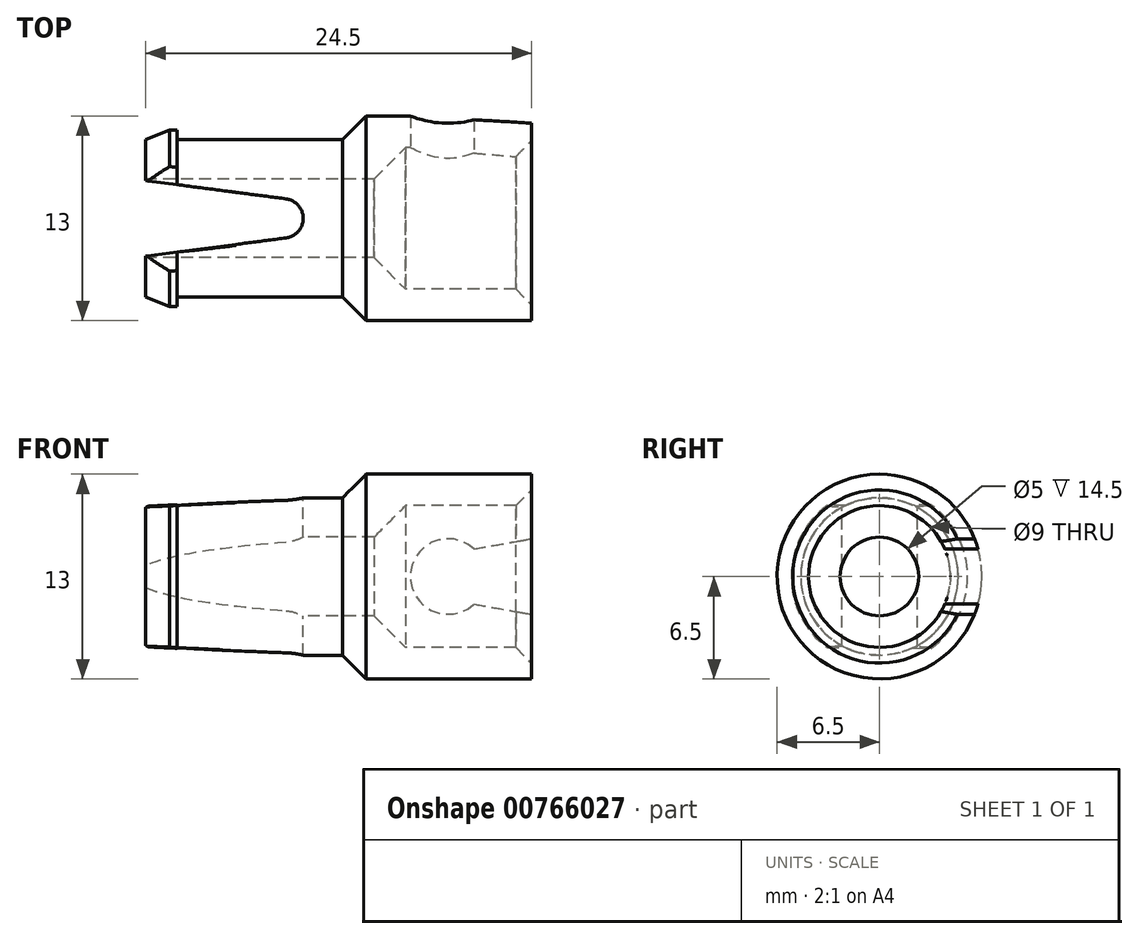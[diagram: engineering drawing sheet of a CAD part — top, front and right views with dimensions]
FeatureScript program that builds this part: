
annotation { "Feature Type Name" : "Feature", "Feature Type Description" : "" }
export const myFeature = defineFeature(function(context is Context, id is Id, definition is map)
    precondition{}
    {
        {
            var Q0;
            Q0=qCreatedBy(makeId("Front.planeOp"),FACE);
            var sketch = newSketch(context, id + "F0", { "sketchPlane" : qUnion([Q0])});
            skLineSegment(sketch, "E0", {"start": v(-22.5, 5) * mm, "end": v(-12, 5) * mm});
            skLineSegment(sketch, "E1", {"start": v(-12, 5) * mm, "end": v(-10.5, 6.5) * mm});
            skLineSegment(sketch, "E2", {"start": v(-10.5, 6.5) * mm, "end": v(0, 6.5) * mm});
            skLineSegment(sketch, "E3", {"start": v(0, 6.5) * mm, "end": v(0, 5.5) * mm});
            skLineSegment(sketch, "E4", {"start": v(0, 5.5) * mm, "end": v(-1, 4.5) * mm});
            skLineSegment(sketch, "E5", {"start": v(-1, 4.5) * mm, "end": v(-8, 4.5) * mm});
            skLineSegment(sketch, "E6", {"start": v(-8, 4.5) * mm, "end": v(-10, 2.5) * mm});
            skLineSegment(sketch, "E7", {"start": v(-10, 2.5) * mm, "end": v(-24.5, 2.5) * mm});
            skLineSegment(sketch, "E8", {"start": v(-22.73, 0) * mm, "end": v(22.26, 0) * mm, "construction": true});
            skLineSegment(sketch, "E9", {"start": v(-22.5, 5) * mm, "end": v(-22.5, 5.6) * mm});
            skLineSegment(sketch, "E10", {"start": v(-22.5, 5.6) * mm, "end": v(-23, 5.6) * mm});
            skLineSegment(sketch, "E11", {"start": v(-23, 5.6) * mm, "end": v(-24.5, 5) * mm});
            skLineSegment(sketch, "E12", {"start": v(-24.5, 5) * mm, "end": v(-24.5, 2.5) * mm});
            skSolve(sketch);
        }
        {
            var Q0;
            Q0=makeQuery(id+"F0.imprint","IMPRINT",FACE,{"disambiguationData":[TD([[makeQuery(id+"F0.imprint","IMPRINT",EDGE,{"derivedFrom":sQuery(id+"F0.wireOp",EDGE,"E0")}),-1.0]])]});
            var Q1;
            Q1=sQuery(id+"F0.wireOp",EDGE,"E8");
            revolve(context, id + "F1", {"surfaceOperationType" : NewSurfaceOperationType.NEW, "entities" : qUnion([Q0]), "axis" : qUnion([Q1]), "revolveType" : RevolveType.FULL});
        }
        {
            var Q0;
            Q0=qCreatedBy(makeId("Front.planeOp"),FACE);
            var sketch = newSketch(context, id + "F2", { "sketchPlane" : qUnion([Q0])});
            skLineSegment(sketch, "E13.0", {"start": v(-12, -5) * mm, "end": v(-12, 5) * mm, "construction": true});
            skLineSegment(sketch, "E14", {"start": v(-10.5, 6.5) * mm, "end": v(0, 6.5) * mm, "construction": true});
            skLineSegment(sketch, "E15", {"start": v(0, -6.5) * mm, "end": v(-10.5, -6.5) * mm, "construction": true});
            skArc(sketch, "E16", {"start": v(-3.66, 1.75) * mm, "mid": v(-7.7, 0) * mm, "end": v(-3.66, -1.75) * mm});
            skPoint(sketch, "E17", {"position": v(-12, 0) * mm});
            skLineSegment(sketch, "E18", {"start": v(-3.66, 1.75) * mm, "end": v(0, 2.4) * mm});
            skLineSegment(sketch, "E19", {"start": v(-3.66, -1.75) * mm, "end": v(0, -2.4) * mm});
            skLineSegment(sketch, "E20", {"start": v(0, 2.4) * mm, "end": v(0, -2.4) * mm});
            skPoint(sketch, "E21", {"position": v(0, 0) * mm});
            skSolve(sketch);
        }
        {
            var Q0;
            Q0 = qSketchRegion(id + "F2", true);
            extrude(context, id + "F3", {"entities" : qUnion([Q0]), "operationType" : NewBodyOperationType.REMOVE, "endBound" : BoundingType.THROUGH_ALL, "oppositeDirection" : true, "depth" : 25 * mm, "offsetDistance" : 25 * mm});
        }
        {
            var Q0;
            Q0=qCreatedBy(makeId("Top.planeOp"),FACE);
            var sketch = newSketch(context, id + "F4", { "sketchPlane" : qUnion([Q0])});
            skLineSegment(sketch, "E22.0", {"start": v(-24.5, -5) * mm, "end": v(-24.5, 5) * mm, "construction": true});
            skLineSegment(sketch, "E23", {"start": v(-24.5, 2.4) * mm, "end": v(-24.5, -2.4) * mm});
            skPoint(sketch, "E24", {"position": v(-24.5, 0) * mm});
            skArc(sketch, "E25", {"start": v(-15.59, -1.24) * mm, "mid": v(-14.5, 0) * mm, "end": v(-15.59, 1.24) * mm});
            skLineSegment(sketch, "E26", {"start": v(-24.5, 2.4) * mm, "end": v(-15.59, 1.24) * mm});
            skLineSegment(sketch, "E27", {"start": v(-24.5, -2.4) * mm, "end": v(-15.59, -1.24) * mm});
            skSolve(sketch);
        }
        {
            var Q0;
            Q0=makeQuery(id+"F4.imprint","IMPRINT",FACE,{"disambiguationData":[TD([[makeQuery(id+"F4.imprint","IMPRINT",EDGE,{"derivedFrom":sQuery(id+"F4.wireOp",EDGE,"E23")}),1.0]])]});
            extrude(context, id + "F5", {"entities" : qUnion([Q0]), "operationType" : NewBodyOperationType.REMOVE, "endBound" : BoundingType.SYMMETRIC, "oppositeDirection" : true, "depth" : 100 * mm, "offsetDistance" : 25 * mm});
        }
        {
            var Q0;
            Q0=makeQuery(id+"F5.boolean.opBoolean","INTERSECT",EDGE,{"disambiguationData":[OD(0.0)],"derivedFrom":[makeQuery(id+"F1.opRevolve","SWEPT_FACE",FACE,{"disambiguationData":[OSD([sQuery(id+"F0.wireOp",EDGE,"E0")])]}),makeQuery(id+"F5.opExtrude","SWEPT_FACE",FACE,{"disambiguationData":[OSD([sQuery(id+"F4.wireOp",EDGE,"E26")])]})]});
            cPoint(context, id + "F6", {"entities" : qUnion([Q0]), "parameter" : 0.5});
        }
        {
            var Q0;
            Q0=makeQuery(id+"F5.boolean.opBoolean","INTERSECT",VERTEX,{"disambiguationData":[OD(0.0)],"derivedFrom":[makeQuery(id+"F1.opRevolve","SWEPT_FACE",FACE,{"disambiguationData":[OSD([sQuery(id+"F0.wireOp",EDGE,"E0")])]}),makeQuery(id+"F1.opRevolve","SWEPT_FACE",FACE,{"disambiguationData":[OSD([sQuery(id+"F0.wireOp",EDGE,"E9")])]}),makeQuery(id+"F5.opExtrude","SWEPT_FACE",FACE,{"disambiguationData":[OSD([sQuery(id+"F4.wireOp",EDGE,"E27")])]})]});
            var Q1;
            Q1 = qCreatedBy(id + "F6" ,VERTEX);
            var Q2;
            Q2=makeQuery(id+"F5.boolean.opBoolean","INTERSECT",VERTEX,{"disambiguationData":[OD(0.0)],"derivedFrom":[makeQuery(id+"F1.opRevolve","SWEPT_FACE",FACE,{"disambiguationData":[OSD([sQuery(id+"F0.wireOp",EDGE,"E0")])]}),makeQuery(id+"F5.opExtrude","SWEPT_FACE",FACE,{"disambiguationData":[OSD([sQuery(id+"F4.wireOp",EDGE,"E25")])]}),makeQuery(id+"F5.opExtrude","SWEPT_FACE",FACE,{"disambiguationData":[OSD([sQuery(id+"F4.wireOp",EDGE,"E27")])]})]});
            cPlane(context, id + "F7", {"entities" : qUnion([Q0, Q1, Q2]), "cplaneType" : CPlaneType.THREE_POINT, "offset" : 25 * mm, "width" : 150 * mm, "height" : 150 * mm});
        }
        {
            var Q0;
            Q0=qCreatedBy(id+"F7.planeOp",FACE);
            var sketch = newSketch(context, id + "F8", { "sketchPlane" : qUnion([Q0])});
            skLineSegment(sketch, "E28.bottom", {"start": v(-19.4, -3.89) * mm, "end": v(-28.8, -3.89) * mm});
            skLineSegment(sketch, "E28.top", {"start": v(-19.4, 5.94) * mm, "end": v(-28.8, 5.94) * mm});
            skLineSegment(sketch, "E28.left", {"start": v(-19.4, -3.89) * mm, "end": v(-19.4, 5.94) * mm});
            skLineSegment(sketch, "E28.right", {"start": v(-28.8, -3.89) * mm, "end": v(-28.8, 5.94) * mm});
            skSolve(sketch);
        }
        {
            var Q0;
            Q0=makeQuery(id+"F8.imprint","IMPRINT",FACE,{"disambiguationData":[TD([[makeQuery(id+"F8.imprint","IMPRINT",EDGE,{"derivedFrom":sQuery(id+"F8.wireOp",EDGE,"E28.bottom")}),-1.0]])]});
            extrude(context, id + "F9", {"entities" : qUnion([Q0]), "operationType" : NewBodyOperationType.REMOVE, "oppositeDirection" : true, "depth" : 25 * mm, "offsetDistance" : 25 * mm});
        }
        {
            var Q0;
            Q0=makeQuery(id+"F5.boolean.opBoolean","INTERSECT",EDGE,{"disambiguationData":[OD(1.0)],"derivedFrom":[makeQuery(id+"F1.opRevolve","SWEPT_FACE",FACE,{"disambiguationData":[OSD([sQuery(id+"F0.wireOp",EDGE,"E0")])]}),makeQuery(id+"F5.opExtrude","SWEPT_FACE",FACE,{"disambiguationData":[OSD([sQuery(id+"F4.wireOp",EDGE,"E26")])]})]});
            cPoint(context, id + "F10", {"entities" : qUnion([Q0]), "parameter" : 0.5});
        }
        {
            var Q0;
            Q0=makeQuery(id+"F5.boolean.opBoolean","INTERSECT",VERTEX,{"disambiguationData":[OD(1.0)],"derivedFrom":[makeQuery(id+"F1.opRevolve","SWEPT_FACE",FACE,{"disambiguationData":[OSD([sQuery(id+"F0.wireOp",EDGE,"E0")])]}),makeQuery(id+"F1.opRevolve","SWEPT_FACE",FACE,{"disambiguationData":[OSD([sQuery(id+"F0.wireOp",EDGE,"E9")])]}),makeQuery(id+"F5.opExtrude","SWEPT_FACE",FACE,{"disambiguationData":[OSD([sQuery(id+"F4.wireOp",EDGE,"E27")])]})]});
            var Q1;
            Q1=makeQuery(id+"F5.boolean.opBoolean","INTERSECT",VERTEX,{"disambiguationData":[OD(1.0)],"derivedFrom":[makeQuery(id+"F1.opRevolve","SWEPT_FACE",FACE,{"disambiguationData":[OSD([sQuery(id+"F0.wireOp",EDGE,"E0")])]}),makeQuery(id+"F5.opExtrude","SWEPT_FACE",FACE,{"disambiguationData":[OSD([sQuery(id+"F4.wireOp",EDGE,"E25")])]}),makeQuery(id+"F5.opExtrude","SWEPT_FACE",FACE,{"disambiguationData":[OSD([sQuery(id+"F4.wireOp",EDGE,"E27")])]})]});
            var Q2;
            Q2 = qCreatedBy(id + "F10" ,VERTEX);
            cPlane(context, id + "F11", {"entities" : qUnion([Q0, Q1, Q2]), "cplaneType" : CPlaneType.THREE_POINT, "offset" : 25 * mm, "width" : 150 * mm, "height" : 150 * mm});
        }
        {
            var Q0;
            Q0=qCreatedBy(id+"F11.planeOp",FACE);
            var sketch = newSketch(context, id + "F12", { "sketchPlane" : qUnion([Q0])});
            skLineSegment(sketch, "E29.bottom", {"start": v(-18.52, 4.86) * mm, "end": v(-33.41, 4.86) * mm});
            skLineSegment(sketch, "E29.top", {"start": v(-18.52, -6.48) * mm, "end": v(-33.41, -6.48) * mm});
            skLineSegment(sketch, "E29.left", {"start": v(-18.52, 4.86) * mm, "end": v(-18.52, -6.48) * mm});
            skLineSegment(sketch, "E29.right", {"start": v(-33.41, 4.86) * mm, "end": v(-33.41, -6.48) * mm});
            skSolve(sketch);
        }
        {
            var Q0;
            Q0=makeQuery(id+"F12.imprint","IMPRINT",FACE,{"disambiguationData":[TD([[makeQuery(id+"F12.imprint","IMPRINT",EDGE,{"derivedFrom":sQuery(id+"F12.wireOp",EDGE,"E29.bottom")}),1.0]])]});
            extrude(context, id + "F13", {"entities" : qUnion([Q0]), "operationType" : NewBodyOperationType.REMOVE, "oppositeDirection" : true, "depth" : 25 * mm, "offsetDistance" : 25 * mm});
        }
    });
